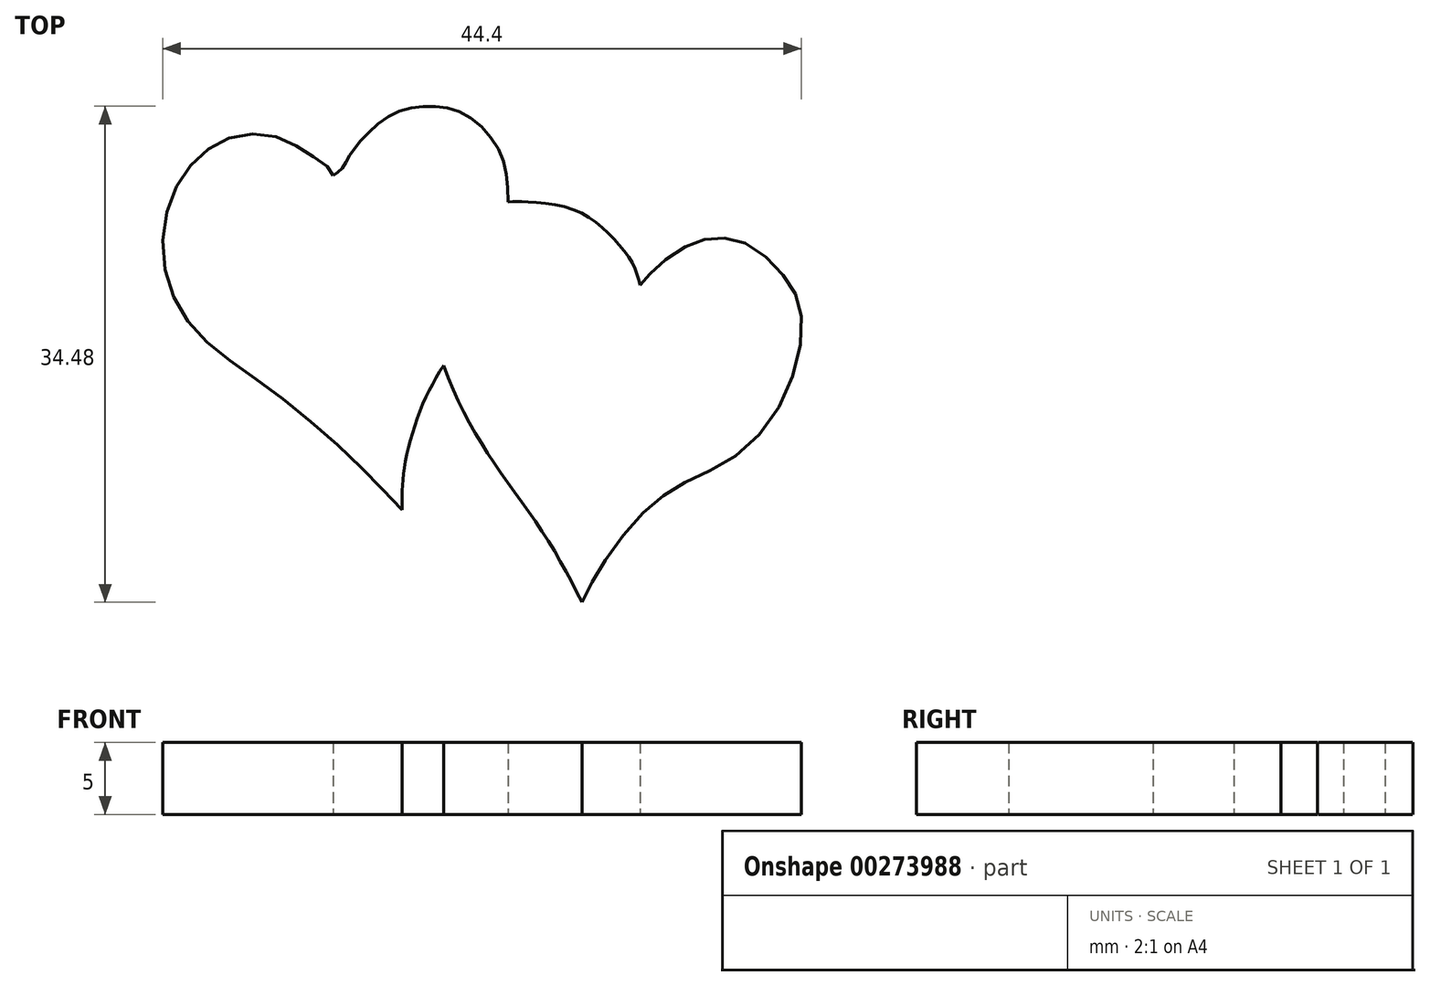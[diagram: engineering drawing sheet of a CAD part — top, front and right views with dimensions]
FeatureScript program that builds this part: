
annotation { "Feature Type Name" : "Feature", "Feature Type Description" : "" }
export const myFeature = defineFeature(function(context is Context, id is Id, definition is map)
    precondition{}
    {
        {
            var Q0;
            Q0=qCreatedBy(makeId("Top.planeOp"),FACE);
            var sketch = newSketch(context, id + "F0", { "sketchPlane" : qUnion([Q0])});
            skFitSpline(sketch, "E0", {"points": [v(13.23, 34.65) * mm, v(12.88, 35.2) * mm, v(11.5, 36.19) * mm, v(9.07, 37.4) * mm, v(5.89, 37.2) * mm, v(3.3, 35.32) * mm, v(1.57, 31.66) * mm, v(1.88, 26.87) * mm, v(4.43, 23.1) * mm, v(8.91, 19.76) * mm, v(14.4, 15.1) * mm, v(18.02, 11.4) * mm], "startDerivative": vector(-7.1, 13.34) * mm, "endDerivative": vector(31, -32.94) * mm});
            skFitSpline(sketch, "E1", {"points": [v(13.23, 34.65) * mm, v(13.76, 35.03) * mm, v(14.24, 35.79) * mm, v(15.04, 36.94) * mm, v(17.14, 38.79) * mm, v(19.79, 39.47) * mm, v(22.53, 38.82) * mm, v(24.85, 36.19) * mm, v(25.4, 32.8) * mm, v(24.93, 27.62) * mm, v(22.3, 23.38) * mm, v(19.63, 19.14) * mm, v(18.14, 14.07) * mm, v(18.02, 11.4) * mm], "startDerivative": vector(12.87, 10.25) * mm, "endDerivative": vector(0.62, -32.72) * mm});
            skFitSpline(sketch, "E2", {"points": [v(34.56, 27.03) * mm, v(34.04, 28.52) * mm, v(32.4, 30.6) * mm, v(29.69, 32.37) * mm, v(26.3, 32.84) * mm, v(25.4, 32.8) * mm, v(23.05, 31.9) * mm, v(20.81, 29.97) * mm, v(20.06, 25.03) * mm, v(21.95, 18.94) * mm, v(24.78, 14.15) * mm, v(27.95, 9.62) * mm, v(30.54, 4.99) * mm], "startDerivative": vector(-6.4, 26.18) * mm, "endDerivative": vector(23.8, -45.9) * mm});
            skFitSpline(sketch, "E3", {"points": [v(34.56, 27.03) * mm, v(35.49, 28.06) * mm, v(37.68, 29.7) * mm, v(39.78, 30.3) * mm, v(42.12, 29.83) * mm, v(44.6, 27.64) * mm, v(45.72, 25.2) * mm, v(45.1, 20.54) * mm, v(41.84, 15.64) * mm, v(37.87, 13.4) * mm, v(34.97, 11.4) * mm, v(31.99, 7.65) * mm, v(30.54, 4.99) * mm], "startDerivative": vector(14.74, 17.88) * mm, "endDerivative": vector(-15.5, -31.56) * mm});
            skSolve(sketch);
        }
        {
            var Q0;
            Q0 = qSketchRegion(id + "F0", true);
            extrude(context, id + "F1", {"entities" : qUnion([Q0]), "depth" : 5 * mm});
        }
    });
